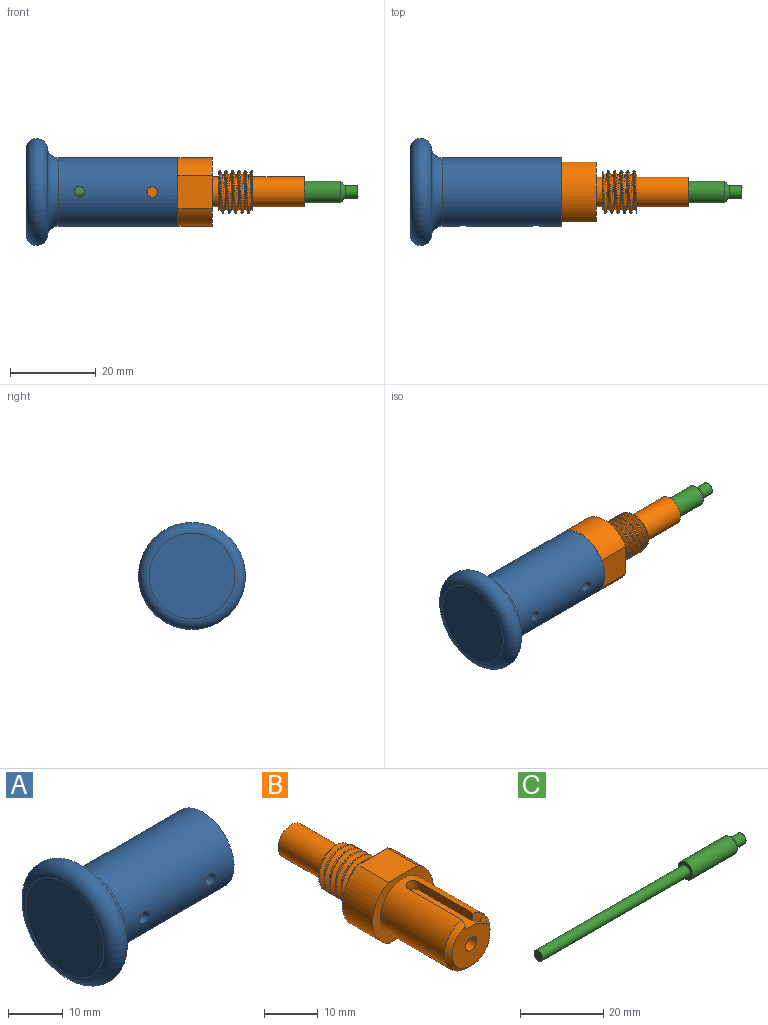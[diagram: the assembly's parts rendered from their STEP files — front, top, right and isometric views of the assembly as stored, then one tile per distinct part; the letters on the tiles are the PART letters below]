
ASSEMBLY  parts=3 mates=3
PART A: 14 faces, bbox 35.5x27.1x27.1 mm
  f0: cylinder r=8mm len=28mm, axis (1,0,0), area 1397.6mm2, adj f1,f8,f9,f13
  f1: cylinder r=1.25mm len=6.9mm, axis (0,-1,0), area 52.5mm2, adj f0,f2,f3,f4
  f2: cone r=0mm half-angle=59deg, axis (0,-1,0), area 0mm2, adj f1,f4
  f3: cone r=0mm half-angle=59deg, axis (0,-1,0), area 0mm2, adj f1,f4
  f4: cylinder r=1.5mm len=8mm, axis (1,0,0), area 70.1mm2, adj f1,f2,f3,f5,f6
  f5: cone r=0mm half-angle=59deg, axis (1,0,0), area 8.2mm2, adj f4
  f6: plane 12x12mm, normal (1,0,0), area 106mm2, adj f4,f7
  f7: cylinder r=6mm len=18.5mm, axis (1,0,0), area 692.5mm2, adj f6,f8,f13
  f8: cylinder r=1.25mm len=2.5mm, axis (0,-1,0), area 15.5mm2, adj f0,f7
  f9: torus R=10.5mm, axis (1,0,0), area 219.8mm2, adj f0,f10
  f10: plane 21x21mm, normal (-1,0,0), area 32.2mm2, adj f9,f11
  f11: torus R=10mm, axis (1,0,0), area 572mm2, adj f10,f12
  f12: plane 20x20mm, normal (-1,0,0), area 314.2mm2, adj f11
  f13: plane 16x16mm, normal (1,0,0), area 88mm2, adj f0,f7
PART B: 28 faces, bbox 16.4x47.9x14.4 mm
  f0: cylinder r=6mm len=17mm, axis (0,1,0), area 594.9mm2, adj f2,f12,f21,f22,f23,f25
  f1: plane 10x9.77mm, normal (0,-1,0), area 66.6mm2, adj f2,f20,f23,f24,f26,f27
  f2: cone r=5mm half-angle=45deg, axis (0,1,0), area 39.8mm2, adj f0,f1,f23,f26
  f3: cone r=0mm half-angle=59deg, axis (0,1,0), area 14.7mm2, adj f19,f20
  f4: cylinder r=5mm len=10mm, axis (0,1,0), area 35.6mm2, adj f5,f6,f17,f18
  f5: plane 9.49x9.49mm, normal (0,-1,0), area 26.3mm2, adj f4,f7,f16,f17,f18
  f6: plane 9.55x9.49mm, normal (0,1,0), area 26.3mm2, adj f4,f14,f16,f17,f18
  f7: cylinder r=3.5mm len=7mm, axis (0,1,0), area 33mm2, adj f5,f13
  f8: plane 8x7.75mm, normal (0,0,1), area 62mm2, adj f9,f11,f12,f13
  f9: cylinder r=8mm len=14mm, axis (0,1,0), area 136.4mm2, adj f8,f10,f12,f13
  f10: plane 8x7.75mm, normal (0,0,-1), area 62mm2, adj f9,f11,f12,f13
  f11: cylinder r=8mm len=14mm, axis (0,1,0), area 136.4mm2, adj f8,f10,f12,f13
  f12: plane 16x14mm, normal (0,-1,0), area 77.5mm2, adj f0,f8,f9,f10,f11
  f13: plane 16x14mm, normal (0,1,0), area 152.1mm2, adj f7,f8,f9,f10,f11
  f14: cylinder r=3.5mm len=12mm, axis (0,-1,0), area 263.9mm2, adj f6,f15
  f15: plane 7x7mm, normal (0,1,0), area 18.8mm2, adj f14,f19
  f16: bspline ~9.67x9.13mm, area 58.3mm2, adj f5,f6,f17,f18
  f17: bspline ~11.55x10mm, area 144.5mm2, adj f4,f5,f6,f16
  f18: bspline ~11.55x10mm, area 144.4mm2, adj f4,f5,f6,f16
  f19: cylinder r=2.5mm len=28mm, axis (0,1,0), area 439.8mm2, adj f3,f15
  f20: cylinder r=1.5mm len=18.9mm, axis (0,-1,0), area 178.1mm2, adj f1,f3
  f21: cylinder r=1.5mm len=3mm, axis (0,0,1), area 8.5mm2, adj f0,f22,f23,f24
  f22: plane 14x1.81mm, normal (-1,0,0), area 25.3mm2, adj f0,f21,f24,f25
  f23: plane 15.03x1.84mm, normal (1,0,0), area 26.6mm2, adj f0,f1,f2,f21,f24
  f24: plane 16.5x3mm, normal (0,0,1), area 48.5mm2, adj f1,f21,f22,f23,f27
  f25: plane 2.86x2.63mm, normal (0,-1,0), area 4.5mm2, adj f0,f22,f26,f27
  f26: cylinder r=1mm len=1.9mm, axis (-0.5,0,-0.87), area 1.6mm2, adj f1,f2,f25,f27
  f27: plane 2.68x1.55mm, normal (0.5,0,0.87), area 2.9mm2, adj f1,f24,f25,f26
PART C: 7 faces, bbox 69x5x5 mm
  f0: plane 3x3mm, normal (-1,0,0), area 7.1mm2, adj f6
  f1: plane 3x3mm, normal (1,0,0), area 7.1mm2, adj f2
  f2: cylinder r=1.5mm len=3mm, axis (1,0,0), area 28.3mm2, adj f1,f3
  f3: cone r=2.5mm half-angle=45deg, axis (-1,0,0), area 17.8mm2, adj f2,f4
  f4: cylinder r=2.5mm len=15mm, axis (1,0,0), area 235.6mm2, adj f3,f5
  f5: plane 5x5mm, normal (-1,0,0), area 12.6mm2, adj f4,f6
  f6: cylinder r=1.5mm len=50mm, axis (1,0,0), area 471.2mm2, adj f0,f5
PLACE A rot(axis=(-0.5,-0.66,-0.56),0deg) t=(-27.76,-3.43,-7.28)mm
PLACE B rot(axis=(0.58,0.58,-0.58),120deg) t=(-3.09,-3.43,-7.28)mm
PLACE C rot(axis=(-0.5,-0.66,-0.56),0deg) t=(7.55,-3.43,-7.28)mm
MATE fastened A.f0 <-> C.f2  axis (1,0,0) through (-47.54,-3.43,-7.28)mm
MATE slider B.f0 <-> A.f0  axis (-1,0,0) through (-20.59,-3.43,-7.28)mm
MATE slider B.f3 <-> C.f2  axis (1,0,0) through (8.91,-3.43,-7.28)mm
